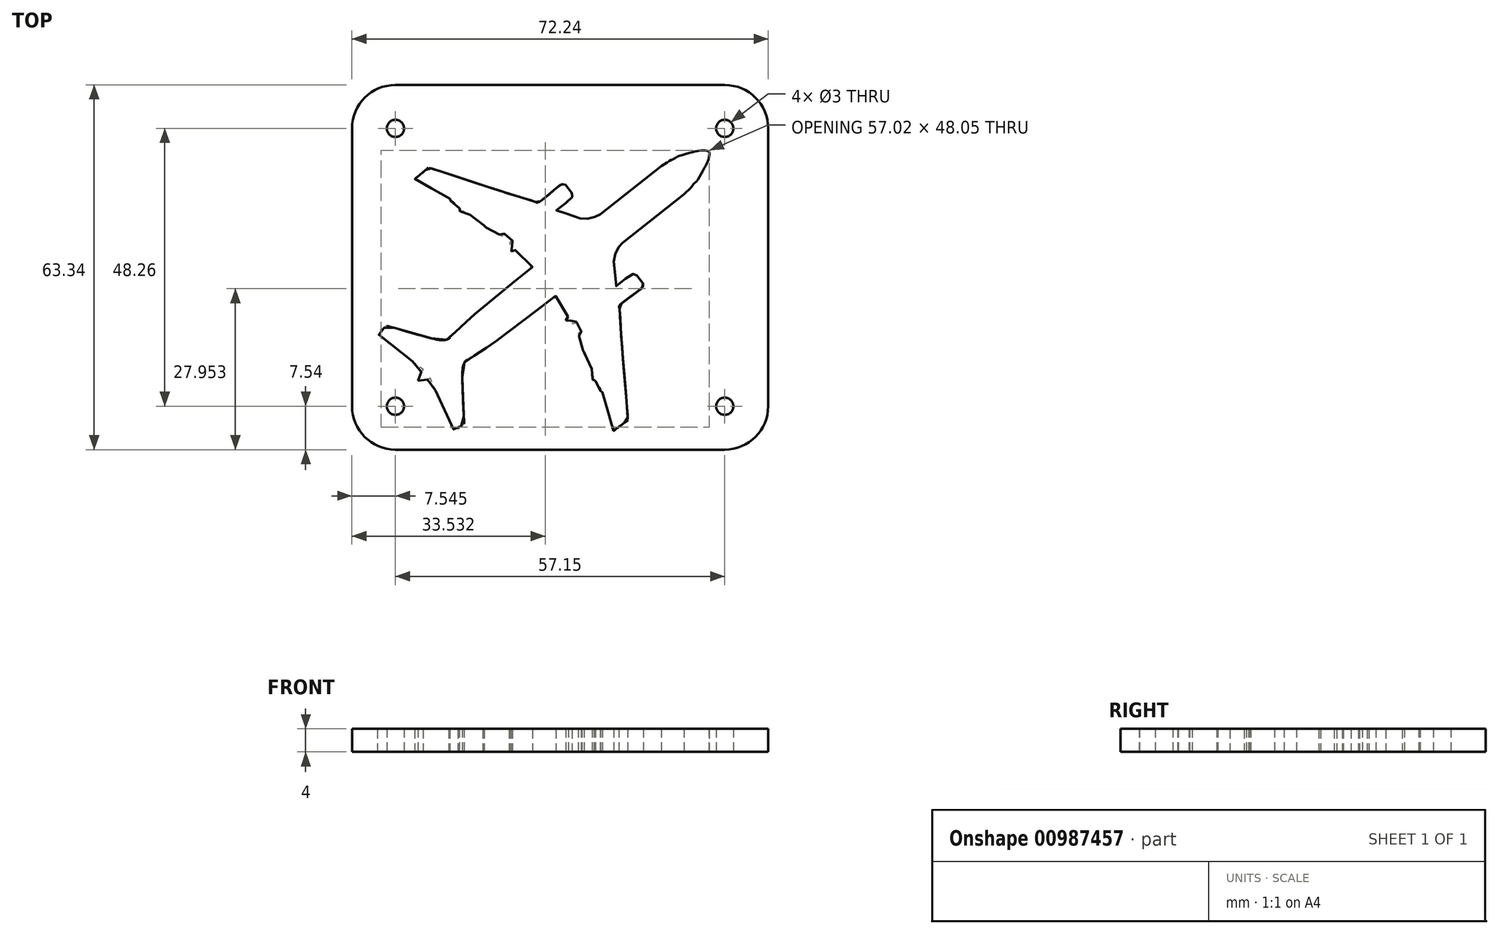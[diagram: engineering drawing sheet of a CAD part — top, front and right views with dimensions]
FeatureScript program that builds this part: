
annotation { "Feature Type Name" : "Feature", "Feature Type Description" : "" }
export const myFeature = defineFeature(function(context is Context, id is Id, definition is map)
    precondition{}
    {
        {
            var Q0;
            Q0=qCreatedBy(makeId("Top.planeOp"),FACE);
            var sketch = newSketch(context, id + "F0", { "sketchPlane" : qUnion([Q0])});
            skLineSegment(sketch, "E0.bottom", {"start": v(-28.57, 31.67) * mm, "end": v(28.58, 31.67) * mm});
            skLineSegment(sketch, "E0.top", {"start": v(-28.58, -31.67) * mm, "end": v(28.57, -31.67) * mm});
            skLineSegment(sketch, "E0.left", {"start": v(-36.11, 24.13) * mm, "end": v(-36.12, -24.13) * mm});
            skLineSegment(sketch, "E0.right", {"start": v(36.12, 24.13) * mm, "end": v(36.11, -24.13) * mm});
            skPoint(sketch, "E0.middle", {"position": v(0, 0) * mm});
            skPoint(sketch, "E1.visualSharp", {"position": v(-36.11, 31.67) * mm});
            skArc(sketch, "E1.filletArc", {"start": v(-28.57, 31.67) * mm, "mid": v(-33.9, 29.46) * mm, "end": v(-36.12, 24.13) * mm});
            skPoint(sketch, "E2.visualSharp", {"position": v(36.12, 31.67) * mm});
            skArc(sketch, "E2.filletArc", {"start": v(36.12, 24.13) * mm, "mid": v(33.9, 29.46) * mm, "end": v(28.58, 31.67) * mm});
            skPoint(sketch, "E3.visualSharp", {"position": v(36.11, -31.67) * mm});
            skArc(sketch, "E3.filletArc", {"start": v(28.57, -31.67) * mm, "mid": v(33.9, -29.46) * mm, "end": v(36.11, -24.13) * mm});
            skPoint(sketch, "E4.visualSharp", {"position": v(-36.12, -31.67) * mm});
            skArc(sketch, "E4.filletArc", {"start": v(-36.12, -24.13) * mm, "mid": v(-33.9, -29.46) * mm, "end": v(-28.58, -31.67) * mm});
            skCircle(sketch, "E5", {"center": v(-28.57, 24.13) * mm, "radius": 1.5 * mm});
            skCircle(sketch, "E6.MirrorC", {"center": v(28.57, 24.13) * mm, "radius": 1.5 * mm});
            skCircle(sketch, "E7.MirrorC", {"center": v(-28.57, -24.13) * mm, "radius": 1.5 * mm});
            skCircle(sketch, "E8.MirrorC", {"center": v(28.57, -24.13) * mm, "radius": 1.5 * mm});
            skLineSegment(sketch, "E9", {"start": v(6.94, 9.2) * mm, "end": v(17.6, 17.59) * mm});
            skFitSpline(sketch, "E10", {"points": [v(17.6, 17.59) * mm, v(19.27, 18.63) * mm, v(19.68, 18.8) * mm, v(20.13, 19.06) * mm, v(20.46, 19.26) * mm, v(22.83, 19.97) * mm, v(24.1, 20.25) * mm, v(25.12, 20.32) * mm, v(25.67, 20.2) * mm, v(25.81, 20.07) * mm], "startDerivative": vector(11.64, 7.76) * mm, "endDerivative": vector(2.07, -2.8) * mm});
            skFitSpline(sketch, "E11", {"points": [v(6.94, 9.2) * mm, v(6.58, 8.95) * mm, v(5.97, 8.72) * mm, v(5.36, 8.51) * mm, v(4.05, 8.38) * mm, v(3.5, 8.49) * mm, v(0.61, 9.5) * mm, v(-0.64, 9.92) * mm, v(-0.6, 9.95) * mm, v(1.87, 11.85) * mm, v(2.12, 12.2) * mm, v(2.17, 12.42) * mm, v(2.14, 12.68) * mm, v(2, 12.99) * mm, v(0.97, 14.31) * mm, v(0.86, 14.36) * mm, v(0.48, 14.43) * mm, v(0.28, 14.39) * mm, v(0.08, 14.33) * mm, v(-0.3, 14.05) * mm, v(-3.85, 11.22) * mm, v(-4.07, 11.26) * mm, v(-4.23, 11.36) * mm, v(-9.17, 12.88) * mm, v(-22.79, 17.29) * mm, v(-22.93, 17.29) * mm, v(-22.98, 17.22) * mm, v(-25.16, 15.35) * mm, v(-25.08, 15.3) * mm, v(-19.13, 11.92) * mm, v(-19.1, 11.92) * mm, v(-19.29, 11.54) * mm, v(-18.95, 11.5) * mm, v(-17.5, 10.27) * mm], "startDerivative": vector(-15.91, -12.36) * mm, "endDerivative": vector(42.27, -39.8) * mm});
            skFitSpline(sketch, "E12", {"points": [v(-17.5, 10.27) * mm, v(-17.6, 10.06) * mm, v(-17.65, 9.87) * mm, v(-17.59, 9.76) * mm, v(-17.44, 9.69) * mm, v(-17.22, 9.7) * mm, v(-16.97, 9.8) * mm, v(-16.78, 9.85) * mm, v(-16.67, 9.8) * mm, v(-13.12, 7.4) * mm, v(-13.12, 7.34) * mm, v(-13.21, 7.3) * mm, v(-13.35, 7.07) * mm, v(-13.33, 6.88) * mm, v(-13.18, 6.86) * mm, v(-13.07, 6.84) * mm, v(-12.87, 6.88) * mm, v(-12.56, 7) * mm, v(-12.52, 7.02) * mm, v(-10.24, 5.46) * mm, v(-10.2, 5.45) * mm, v(-10.13, 5.47) * mm, v(-9.82, 5.87) * mm, v(-9.75, 5.89) * mm, v(-9.69, 5.86) * mm, v(-9.66, 5.78) * mm, v(-8.39, 4.76) * mm, v(-8.3, 4.66) * mm, v(-8.29, 4.6) * mm, v(-8.78, 4.15) * mm, v(-8.75, 4.03) * mm, v(-8.39, 3.72) * mm, v(-8.19, 3.41) * mm, v(-8.3, 3.25) * mm, v(-8.47, 3.06) * mm, v(-8.48, 2.89) * mm, v(-8.4, 2.79) * mm, v(-8.22, 2.9) * mm, v(-8.06, 2.97) * mm, v(-7.88, 3.12) * mm, v(-7.83, 3.06) * mm, v(-7.75, 2.94) * mm, v(-4.75, 0) * mm, v(-4.8, -0.06) * mm, v(-4.97, -0.16) * mm, v(-15.28, -8.5) * mm, v(-15.44, -8.66) * mm, v(-15.72, -8.93) * mm, v(-17.09, -10.18) * mm, v(-18, -11.11) * mm, v(-18.95, -12.1) * mm, v(-19.49, -12.52) * mm, v(-20.23, -12.66) * mm, v(-21.84, -12.45) * mm, v(-29.96, -10.2) * mm, v(-30.14, -10.16) * mm, v(-30.23, -10.2) * mm, v(-30.58, -10.52) * mm, v(-31.64, -11.3) * mm, v(-31.6, -11.49) * mm, v(-31.55, -11.61) * mm, v(-23.78, -17.68) * mm, v(-23.73, -17.74) * mm, v(-23.93, -17.95) * mm, v(-24.31, -18.5) * mm, v(-24.56, -19.15) * mm, v(-24.64, -19.67) * mm], "startDerivative": vector(-10.06, -20.4) * mm, "endDerivative": vector(-3.06, -33.6) * mm});
            skFitSpline(sketch, "E13.MirrorCS", {"points": [v(6.15, -19.75) * mm, v(5.92, -19.8) * mm, v(5.72, -19.8) * mm, v(5.63, -19.71) * mm, v(5.6, -19.55) * mm, v(5.65, -19.34) * mm, v(5.8, -19.12) * mm, v(5.9, -18.95) * mm, v(5.89, -18.83) * mm, v(4.38, -14.82) * mm, v(4.32, -14.8) * mm, v(4.26, -14.88) * mm, v(4, -14.97) * mm, v(3.83, -14.9) * mm, v(3.84, -14.75) * mm, v(3.85, -14.64) * mm, v(3.94, -14.46) * mm, v(4.12, -14.18) * mm, v(4.16, -14.15) * mm, v(3.17, -11.57) * mm, v(3.16, -11.52) * mm, v(3.2, -11.46) * mm, v(3.66, -11.25) * mm, v(3.7, -11.19) * mm, v(3.68, -11.12) * mm, v(3.62, -11.07) * mm, v(2.92, -9.6) * mm, v(2.85, -9.48) * mm, v(2.8, -9.46) * mm, v(2.24, -9.84) * mm, v(2.13, -9.79) * mm, v(1.9, -9.35) * mm, v(1.66, -9.09) * mm, v(1.47, -9.16) * mm, v(1.25, -9.28) * mm, v(1.08, -9.25) * mm, v(1, -9.15) * mm, v(1.16, -9) * mm, v(1.26, -8.86) * mm, v(1.45, -8.72) * mm, v(1.4, -8.66) * mm, v(1.3, -8.55) * mm, v(-0.85, -4.95) * mm, v(-0.92, -4.97) * mm, v(-1.06, -5.13) * mm, v(-11.58, -13.2) * mm, v(-11.77, -13.31) * mm, v(-12.1, -13.52) * mm, v(-13.63, -14.56) * mm, v(-14.76, -15.23) * mm, v(-15.94, -15.92) * mm, v(-16.48, -16.34) * mm, v(-16.78, -17.03) * mm, v(-16.96, -18.65) * mm, v(-16.66, -27.07) * mm, v(-16.68, -27.25) * mm, v(-16.74, -27.33) * mm, v(-17.13, -27.6) * mm, v(-18.14, -28.44) * mm, v(-18.31, -28.37) * mm, v(-18.42, -28.28) * mm, v(-22.5, -19.31) * mm, v(-22.54, -19.25) * mm, v(-22.8, -19.4) * mm, v(-23.42, -19.63) * mm, v(-24.1, -19.73) * mm, v(-24.64, -19.67) * mm], "startDerivative": vector(-22.18, -5) * mm, "endDerivative": vector(-33.39, 4.9) * mm});
            skFitSpline(sketch, "E14.MirrorCS", {"points": [v(21.48, 12.66) * mm, v(22.88, 14.04) * mm, v(23.14, 14.4) * mm, v(23.5, 14.78) * mm, v(23.77, 15.05) * mm, v(25.02, 17.2) * mm, v(25.6, 18.35) * mm, v(25.9, 19.34) * mm, v(25.91, 19.9) * mm, v(25.81, 20.07) * mm], "startDerivative": vector(10.27, 9.5) * mm, "endDerivative": vector(-2.24, 2.67) * mm});
            skLineSegment(sketch, "E15.MirrorCS", {"start": v(10.82, 4.27) * mm, "end": v(21.48, 12.66) * mm});
            skFitSpline(sketch, "E16.MirrorCS", {"points": [v(10.82, 4.27) * mm, v(10.5, 3.97) * mm, v(10.14, 3.43) * mm, v(9.79, 2.89) * mm, v(9.36, 1.65) * mm, v(9.33, 1.09) * mm, v(9.64, -1.96) * mm, v(9.75, -3.28) * mm, v(9.8, -3.25) * mm, v(12.22, -1.29) * mm, v(12.62, -1.13) * mm, v(12.85, -1.13) * mm, v(13.09, -1.22) * mm, v(13.35, -1.43) * mm, v(14.4, -2.74) * mm, v(14.43, -2.86) * mm, v(14.4, -3.24) * mm, v(14.32, -3.42) * mm, v(14.21, -3.61) * mm, v(13.85, -3.92) * mm, v(10.27, -6.7) * mm, v(10.25, -6.92) * mm, v(10.31, -7.1) * mm, v(10.63, -12.26) * mm, v(11.73, -26.53) * mm, v(11.7, -26.67) * mm, v(11.62, -26.7) * mm, v(9.29, -28.38) * mm, v(9.27, -28.3) * mm, v(7.36, -21.72) * mm, v(7.37, -21.68) * mm, v(6.96, -21.78) * mm, v(7, -21.44) * mm, v(6.15, -19.75) * mm], "startDerivative": vector(-15.75, -12.58) * mm, "endDerivative": vector(-28.8, 50.41) * mm});
            skSolve(sketch);
        }
        {
            var Q0;
            Q0=makeQuery(id+"F0.imprint","IMPRINT",FACE,{"disambiguationData":[TD([[makeQuery(id+"F0.imprint","IMPRINT",EDGE,{"derivedFrom":sQuery(id+"F0.wireOp",EDGE,"E0.bottom")}),-1.0]])]});
            extrude(context, id + "F1", {"entities" : qUnion([Q0]), "depth" : 4 * mm, "offsetDistance" : 25 * mm});
        }
    });
